# Revit family: Lighting - Luminii - Kilo - Graze Wash - Static White - Array
name_source: partatom
category: Lighting Fixtures
units: mm (PartAtom-declared; Revit-internal decimal feet)

## family parameters
Cut with Voids When Loaded = No
Host = Face
Light Source = No
OmniClass Number = 23.80.70.11.14.21
OmniClass Title = Spots and Tracklight Specialties
Part Type = Normal
Room Calculation Point = No
Round Connector Dimension = Use Diameter
Shared = Yes

## types (4) — shared parameters
Assembly Code = D5020230
C Tilt Base Offset = 1 1/16"
CCT = 3000K
Current Amps = 50 A
Default Elevation = 0"
Description = Linear Valance Illumination System
Environment = Indoor
Finish = Metal - Luminii - Silver Anodized Aluminum
Frequency = 60 Hz
Has Battery Backup = No
Has Dimming = Yes
Housing Protection Rating = IP20 Dry/IP66 Wet Series
Initial Color Comments = Perfomance based on 3000K Photometric Web File
Instruction Sheet Link = https://www.luminii.com
Keynote = 26 50 00
Lamp = LED
Lamp Life = 1
Lens Material = Plastic - Luminii - Frosted Lens
Load Classification = Lighting
Manufacturer = Luminii
Model = KGW
Mounting Method = Surface Mount
Number of Poles = 1
Operating Temperature = Consult Manufacturer Website for more Information
Phase = 1
Power Factor = 1
Power Source Type = Driver
Product Documentation Link = https://www.luminii.com
Product Name = Kilo Graze-Wash - Static White
Product Page URL = https://www.luminii.com
URL = https://www.luminii.com
Version = 2020 - v1.0a
Voltage = 120 V
Voltage Comments = 120VAC - 277VAC
Warranty URL = https://www.luminii.com
Width = 1 3/8"

## per-type parameters (varying)
| type | Apparent Load | Depth | Fixed Clip Option | High Color Quality | High Efficacy | Lumen Output | Tilt Base Option | Wattage Comments |
| Kilo Graze-Wash - High Color Quality - Tilt Base | 3 VA | 2 5/16" | No | Yes | No | 166 lm/ft | Yes | 2.8 W/ft |
| Kilo Graze-Wash - High Color Quality - Fixed Clip | 3 VA | 1 15/32" | Yes | Yes | No | 166 lm/ft | No | 2.8 W/ft |
| Kilo Graze-Wash - High Efficacy - Tilt Base | 2 VA | 2 5/16" | No | No | Yes | 162 lm/ft | Yes | 1.9 W/ft |
| Kilo Graze-Wash - High Efficacy - Fixed Clip | 2 VA | 1 15/32" | Yes | No | Yes | 162 lm/ft | No | 1.9 W/ft |

## geometry (parser evidence)
native form markers: Sweep x8
no freeform markers — native parametric forms only
